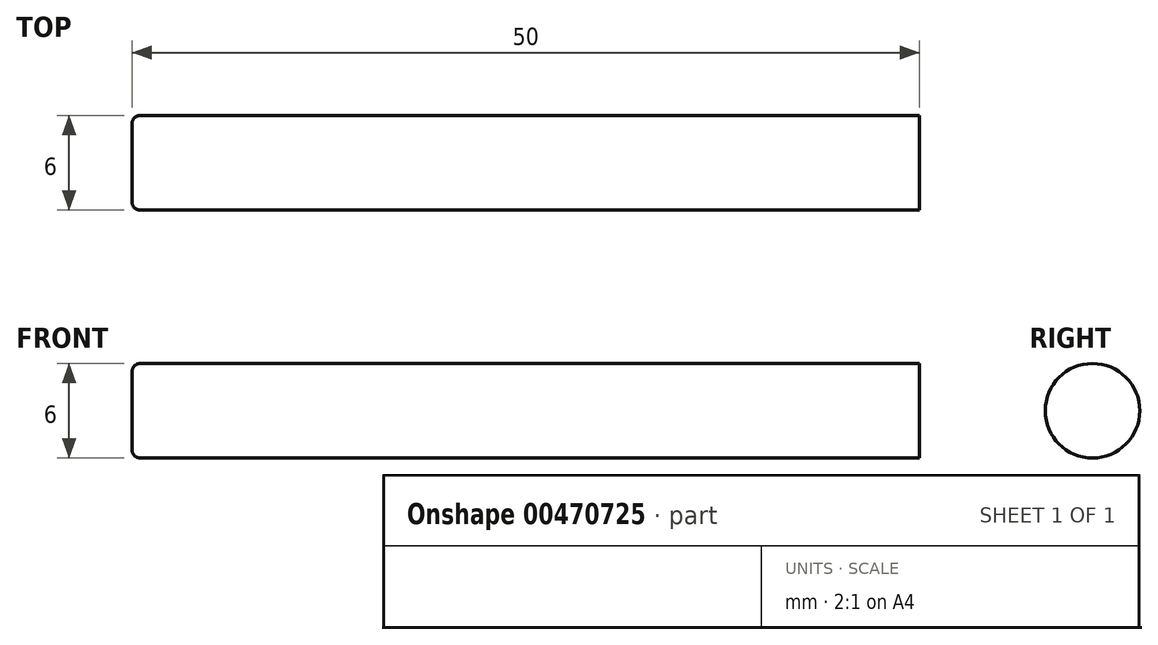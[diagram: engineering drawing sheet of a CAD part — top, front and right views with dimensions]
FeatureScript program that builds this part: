
annotation { "Feature Type Name" : "Feature", "Feature Type Description" : "" }
export const myFeature = defineFeature(function(context is Context, id is Id, definition is map)
    precondition{}
    {
        {
            var Q0;
            Q0=qCreatedBy(makeId("Top.planeOp"),FACE);
            var sketch = newSketch(context, id + "F0", { "sketchPlane" : qUnion([Q0])});
            skLineSegment(sketch, "E0.bottom", {"start": v(-25, 0) * mm, "end": v(25, 0) * mm});
            skLineSegment(sketch, "E0.top", {"start": v(-24.5, 3) * mm, "end": v(25, 3) * mm});
            skLineSegment(sketch, "E0.left", {"start": v(-25, 0) * mm, "end": v(-25, 2.5) * mm});
            skLineSegment(sketch, "E0.right", {"start": v(25, 0) * mm, "end": v(25, 3) * mm});
            skPoint(sketch, "E1.visualSharp", {"position": v(-25, 3) * mm});
            skArc(sketch, "E1.filletArc", {"start": v(-24.5, 3) * mm, "mid": v(-24.85, 2.85) * mm, "end": v(-25, 2.5) * mm});
            skSolve(sketch);
        }
        {
            var Q0;
            Q0=makeQuery(id+"F0.imprint","IMPRINT",FACE,{"disambiguationData":[TD([[makeQuery(id+"F0.imprint","IMPRINT",EDGE,{"derivedFrom":sQuery(id+"F0.wireOp",EDGE,"E0.bottom")}),1.0]])]});
            var Q1;
            Q1=sQuery(id+"F0.wireOp",EDGE,"E0.bottom");
            revolve(context, id + "F1", {"entities" : qUnion([Q0]), "axis" : qUnion([Q1]), "revolveType" : RevolveType.FULL});
        }
    });
